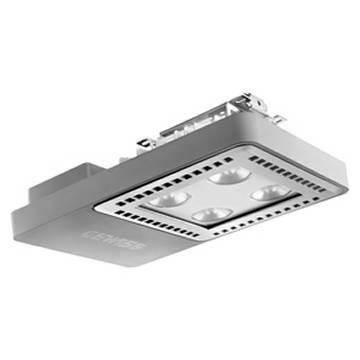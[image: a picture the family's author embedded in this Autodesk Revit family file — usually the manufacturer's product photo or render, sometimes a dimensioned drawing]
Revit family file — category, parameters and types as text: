
# Revit family: Lighting-Industriale-GEWISS-SMART[4]ATEX_APPARECCHI-LED_1M
name_source: partatom
category: Apparecchi per illuminazione
units: mm (PartAtom-declared; Revit-internal decimal feet)

## family parameters
Basato su piano di lavoro = Sì
Condiviso = No
Numero OmniClass = 23.80.00.00
Punto di calcolo locali = No
Quota connettore circolare = Usa diametro
Sempre verticale = No
Sorgente d'illuminazione = No
Taglio con vuoti quando caricato = No
Tipo di parte = Normale
Titolo OmniClass = Electric Power and Lighting

## types (1)
- Lighting-Industriale-GEWISS-SMART[4]ATEX_APPARECCHI-LED_1M
    Alimentatore = Incluso
    Apparecchio a ridotta temperatura superficiale = Si
    Applicazione = Interno
    Cablaggio = Cablaggio singolo con cavo antirespirazione che esce da PG metallico (NO Connettore)
    Caratteristiche elettriche e gestione della luce = -
    Caratteristiche ottiche e illuminotecniche = -
    Carico apparente = 50 VA
    Catalogo = LIGHTING
    Certificazione DIN 18032-3 = -
    Certificazioni e classificazioni = -
    Classe fotobiologica = RG0
    Classe isolamento = I
    Classificazione = Lighting
    Classificazione: = ATEX: II 3 G Ex nR IIC T6 Gc - II 3 D Ex tc IIIC T65°C Dc
    Codice Electrocod = 2444
    Codice digitale univoco (Datamatrix) = Datamatrix
    Colore = Grigio RAL 7035
    Commenti sul wattaggio = 50W
    Contesto = Illuminazione di logistiche e locali produttivi industriali
    Controllo abbagliamento e luminanza = UGR - 25
    Corpo = PA6 “Halogen Free” caricato fibra vetro
    Descrizione = SMART[4]LB 1M ST.AL.ON/OFF ATEX 90° 57K
    Dispositivo di protezione = DM 6 kV / CM 10 kV
    Distanza tot_plafoniera = 74 mm  [stored 0.242782 ft]
    Durata di vita = L90B10 (Tq+25°C) = 100.000 h - L90B10 (Tq+40°C) = 50.000 h
    Efficienza luminosa (lm/W) = 142
    Finitura colore = Grigio RAL 7035
    Fissaggio = -
    Frequenza nominale (Hz) = 50/60 Hz
    Gancio di chiusura = -
    Garanzia = 5 anni
    Grado di protezione = IP66
    Gruppo ottico = Riflettore in PC metallizzato e lenti in PMMA
    Guarnizioni = tipo siliconico antinvecchiamento
    IDF = 60a8a722-c8ac-4f53-b8cc-3a708bea06e4
    IDT = b95782d405ee4ca1a3b4b3dc6b47d217
    IPEA = -
    Immagine tipo = GWL1071.jpg
    Inclinazione = Con accessorio staffa
    Indice di resa cromatica = CRI-80
    Informazioni generali = -
    Installazione e manutenzione = -
    Lampada = LED
    Larghezza = 253 mm  [stored 0.830052 ft]
    Lumen output (lm) = 9100
    Lunghezza = 383 mm  [stored 1.25656 ft]
    Materiali = -
    Modello = GWS4120FP857
    Motore = <Per categoria>
    Norma di riferimento = EN 60079-0 ; EN 60079-15 ; EN 60079-31 ; EN 60598-1 ; EN 60598-2-1
    Ottica = 90°
    Peso (kg): = 3,5
    Plafoniera = <Per categoria>
    Potenza di sistema = 64W
    Produttore = GEWISS S.p.A.
    Prospetto di default = 1219 mm
    Raggio led = 30 mm  [stored 0.0984252 ft]
    Resistenza agli urti = IK08
    Resistenza al filo incandescente = 850 °C
    Scheda Tecnica = https://www.gewiss.com
    Schermo = Vetro Temprato Spessore 4mm
    Sistema di controllo = ON / OFF
    Sistema di controllo : = ON / OFF
    Sostituibilità gruppo ottico = Non sostituibile
    Sostituibilità piastra di cablaggio = Non sostituibile
    Spessore plafoniera = 40 mm
    Superficie massima esposta al vento : = 0,097 m²
    Temperatura di colore = 5700K
    Temperatura di esercizio = +5°C / +40 °C
    Temperatura di stoccaggio = -40 +70 °C
    Tensione di alimentazione = 220 - 240 V
    Tipo di apparecchio = Riflettore industriale a LED&nbsp;
    Tipo di installazione e montaggio = Plafone - Parete - Sospensione
    Tipologia sorgente luminosa = LED - Non sostituibile
    Tolleranza cromatica = SDCM = 3
    Trasformatore = <Per categoria>
    URL = https://www.gewiss.com
    Vano di alimentazione = Integrato
    Versione file RFA = 20.11
    Vetro acceso = Lampada accesa
    Viti esterne = Acciaio inox
    Voltaggio = 230 V

note: [stored X ft] marks values corroborated as IEEE doubles in the binary element streams (Revit-internal decimal feet)

## geometry (parser evidence)
native form markers: Blend x4
no freeform markers — native parametric forms only
